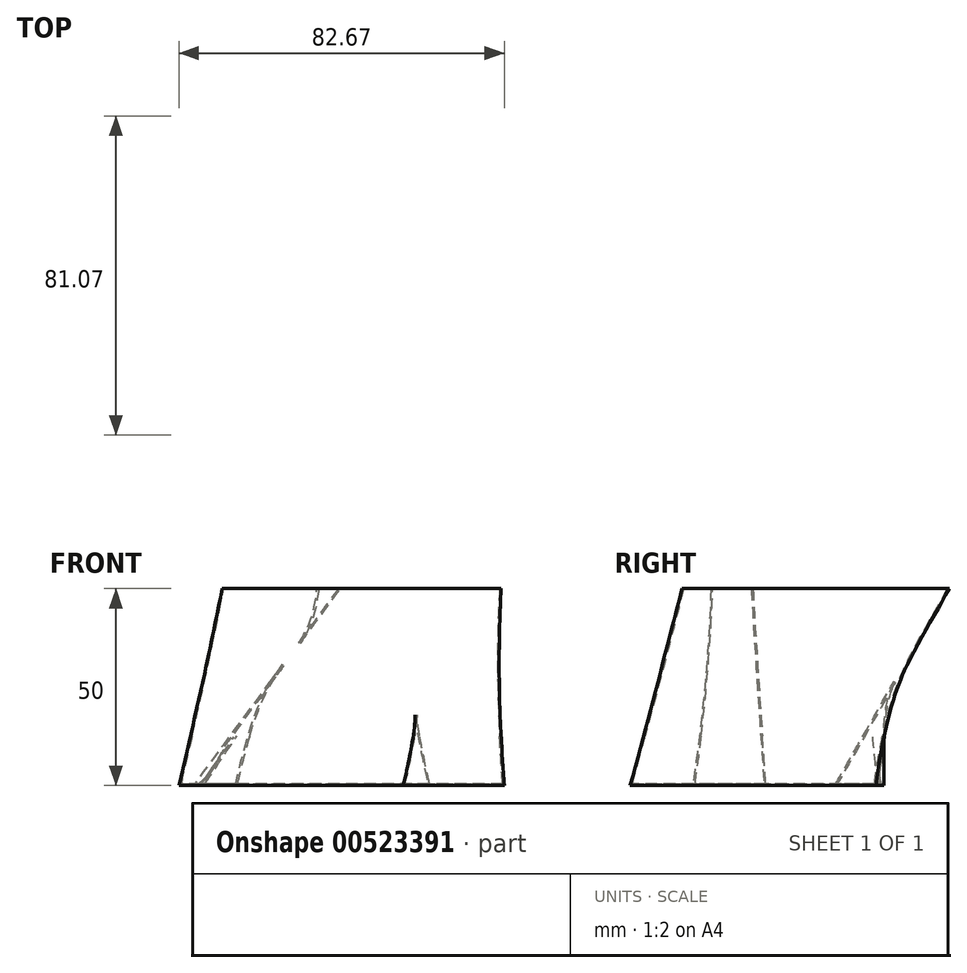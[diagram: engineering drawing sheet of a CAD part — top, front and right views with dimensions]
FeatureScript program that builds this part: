
annotation { "Feature Type Name" : "Feature", "Feature Type Description" : "" }
export const myFeature = defineFeature(function(context is Context, id is Id, definition is map)
    precondition{}
    {
        {
            var Q0;
            Q0=qCreatedBy(makeId("Top.planeOp"),FACE);
            var sketch = newSketch(context, id + "F0", { "sketchPlane" : qUnion([Q0])});
            skFitSpline(sketch, "E0", {"points": [v(0, 0) * mm, v(-39.94, 0) * mm, v(-25.63, 26.13) * mm, v(-36.28, 43.44) * mm, v(5.66, 31.45) * mm, v(37.61, 41.1) * mm, v(38.28, 4.83) * mm, v(17.3, -20.14) * mm, v(23.3, 12.15) * mm, v(0, 0) * mm]});
            skSolve(sketch);
        }
        {
            var Q0;
            Q0=qCreatedBy(makeId("Top.planeOp"),FACE);
            cPlane(context, id + "F1", {"entities" : qUnion([Q0]), "cplaneType" : CPlaneType.OFFSET, "offset" : 50 * mm, "width" : 150 * mm, "height" : 150 * mm});
        }
        {
            var Q0;
            Q0=qCreatedBy(id+"F1.planeOp",FACE);
            var sketch = newSketch(context, id + "F2", { "sketchPlane" : qUnion([Q0])});
            skFitSpline(sketch, "E1", {"points": [v(0, 0) * mm, v(-28.96, 16.14) * mm, v(0, 37.78) * mm, v(-4.66, 58.75) * mm, v(33.95, 36.78) * mm, v(34.95, -7.82) * mm, v(11.32, 9.82) * mm, v(0, 0) * mm]});
            skSolve(sketch);
        }
        {
            var Q0;
            Q0=makeQuery(id+"F0.imprint","IMPRINT",FACE,{"disambiguationData":[TD([[makeQuery(id+"F0.imprint","IMPRINT",EDGE,{"derivedFrom":sQuery(id+"F0.wireOp",EDGE,"E0")}),-1.0]])]});
            var Q1;
            Q1=makeQuery(id+"F2.imprint","IMPRINT",FACE,{"disambiguationData":[TD([[makeQuery(id+"F2.imprint","IMPRINT",EDGE,{"derivedFrom":sQuery(id+"F2.wireOp",EDGE,"E1")}),-1.0]])]});
            loft(context, id + "F3", {"sheetProfilesArray" : [{ "sheetProfileEntities" : qUnion([Q0]) }, { "sheetProfileEntities" : qUnion([Q1]) }]});
        }
        {
            var Q0;
            Q0=makeQuery(id+"F3.opLoft","CAP_FACE",FACE,{"disambiguationData":[OSD([makeQuery(id+"F2.imprint","IMPRINT",FACE,{"disambiguationData":[TD([[makeQuery(id+"F2.imprint","IMPRINT",EDGE,{"derivedFrom":sQuery(id+"F2.wireOp",EDGE,"E1")}),-1.0]])]})])],"isStart":true});
            shell(context, id + "F4", {"entities" : qUnion([Q0]), "thickness" : 0.4 * mm});
        }
    });
